# Revit family: 355394xx0--Vitreous china bidet 530x355  - Victoria - 355394xx0
name_source: partatom
category: Plumbing Fixtures
units: mm (PartAtom-declared; Revit-internal decimal feet)

## family parameters
Always vertical = Yes
Cut with Voids When Loaded = No
OmniClass Number = 23.45.05.14.27
OmniClass Title = Bidets
Part Type = Normal
Room Calculation Point = No
Round Connector Dimension = Use Diameter
Shared = No
Work Plane-Based = No

## types (2) — shared parameters
BIMobject category = Bidets
Description = Vitreous china bidet
Drain Diameter = 102 mm
Edition number = 1
Height = 385 mm  [stored 1.26312 ft]
IFC Classification = Sanitary Terminal
Installation type = Floorstanding
Length = 355 mm
Manufacturer URL = http://www.roca.com
Manufacturer name = Roca
Model = 355394..0
NBS Reference Code = 35-06-11
NBS Reference Description = Bidets
Nominal height = 38500
Nominal width = 53000
OmniClass Code = 23-31 23 00
OmniClass Description = Bidets
Product Guid = c32b9806-f7dd-4583-ad6a-ac22ebad9be8
Product data url = http://bimobject.com
Product family = Victoria|Laura
Product group = BIDETS
QR code = https://www.roca.com
Secondary Material = Chrome - Victoria - Roca
Shape = Round
Taphole configuration = 1 Taphole
Technical description = http://www.roca.com
UNSPSC Code = 30181502
URL = http://www.export.roca.com
Uniclass 1.4 Code = L7215
Uniclass 1.4 Description = Bidets
Uniclass 2.0 Code = PR-35-06-11
Uniclass 2.0 Description = Bidets
Water Inlet Diameter = 55 mm  [stored 0.180446 ft]
Width = 530 mm  [stored 1.73885 ft]
zero-valued in all types: Weight Net (Kg)

## per-type parameters (varying)
| type | Imported Category Visibility 01 | Imported Category Visibility 02 | Primary Material | Product SKU |
| 355394000 White | Yes | No | White - Victoria - Roca | 355394000 |
| 355394170 Pergamon | No | Yes | Pergamon - Victoria - Roca | 355394170 |

note: [stored X ft] marks values corroborated as IEEE doubles in the binary element streams (Revit-internal decimal feet)

## geometry (parser evidence)
native form markers: Blend x2, Extrusion x1, Sweep x3
no freeform markers — native parametric forms only
